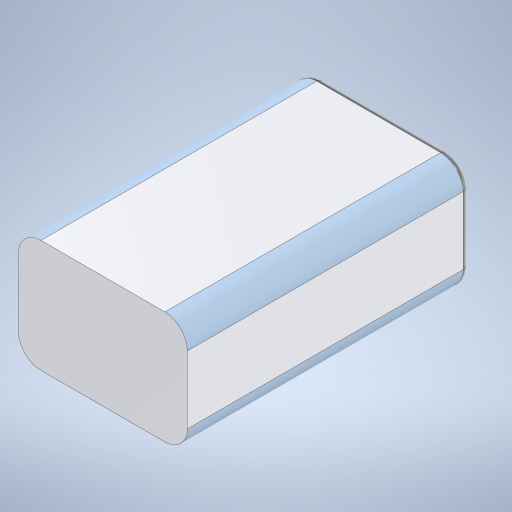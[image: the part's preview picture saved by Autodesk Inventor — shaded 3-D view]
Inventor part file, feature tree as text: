
AUTODESK INVENTOR PART (.ipt)
format: ipt  version: 2023 (Build 270158000, 158)  size: 672,768 bytes
history: native  units: in
note: dims shown in document units (in); Inventor stores cm internally (conversion verified against a paired STEP export)
features: sketch x10, extrude x6, fillet x5, hole x2, other x2
ambient origin geometry x8: Origin, YZ Plane, XZ Plane, XY Plane, X Axis, Y Axis, Z Axis, Center Point
bodies: Solid1 (feature_tree)
feature tree (25):
  extrude  "Extrusion1"  Depth=3.937in
  fillet  "Fillet1"  Radius=9.8425in
  fillet  "Fillet2"  Radius=0.7874in
  fillet  "Fillet3"  Radius=0.7874in
  fillet  "Fillet4"  Radius=0.7874in
  fillet  "Fillet5"  Radius=0.7874in
  extrude  "Extrusion2"  Depth=0.1969in
  extrude  "Extrusion3"  Depth=0.1969in
  extrude  "Extrusion4"  Depth=0.3937in
  extrude  "Extrusion5"  Depth=0.1969in
  hole  "Hole1"  [1 undecoded]
  hole  "Hole2"  [1 undecoded]
  other  "Decal1"
  sketch  "Sketch9"  dims[d23=0.9843in]
  extrude  "Extrusion6"  Depth=2.7559in
  sketch  "Sketch1"  dims[d0=5.9055in d1=3.937in d2=9.8425in d3=0.0in d4=0.7874in d5=0.7874in d6=0.7874in d7=0.7874in]
  sketch  "Sketch2"  dims[d8=0.1969in d9=0.9843in]
  sketch  "Sketch3"  dims[d10=0.1969in d11=0.1969in]
  sketch  "Sketch4"  dims[d12=0.9843in d13=0.3937in]
  sketch  "Sketch5"  dims[d14=0.3937in d15=0.1969in]
  sketch  "Sketch6"  dims[d16=0.9843in d17=0.1969in]
  sketch  "Sketch7"  dims[d18=0.1969in d19=0.0in d20=1.9685in]
  sketch  "Sketch8"  dims[d21=1.5748in d22=2.7559in]
  other  "Image1"
  sketch  "Sketch10"  dims[d24=0.9843in d25=0.1181in d26=0.0in d27=0.5906in d28=0.5906in d29=0.0in d30=0.7874in d31=0.6693in d32=0.1575in d33=0.0in d34=0.3979in d35=0.9449in d36=0.1575in d37=0.0787in d38=90.0deg d39=1.1024in d40=0.8108in d41=0.4192in d42=0.9449in d43=0.1575in d44=0.0787in d45=90.0deg d46=1.1024in d47=0.8108in d50=0.748in d51=0.748in d52=1.9685in d53=0.0in d54=0.0344in]
note: 2 required parameter values undecoded (feature->parameter linkage not recoverable at this tier; creation-order binding heuristic only, values carry confidence <= 0.55)
